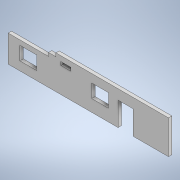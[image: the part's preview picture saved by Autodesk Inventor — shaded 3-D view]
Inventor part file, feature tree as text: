
AUTODESK INVENTOR PART (.ipt)
format: ipt  version: 2020.1 (Build 241239000, 239)  size: 135,680 bytes
history: native  units: in
note: dims shown in document units (in); Inventor stores cm internally (conversion verified against a paired STEP export)
features: extrude x1, sketch x1
ambient origin geometry x8: Origin, YZ Plane, XZ Plane, XY Plane, X Axis, Y Axis, Z Axis, Center Point
bodies: Solid1 (feature_tree)
feature tree (2):
  extrude  "Extrusion1"  Depth=96.0in
  sketch  "Sketch1"  dims[d0=144.0in d1=96.0in d2=26.0in d3=108.0in d4=222.0in d5=120.0in d6=54.0in d7=85.0in d8=180.0in d9=120.0in d10=12.0in d11=36.0in d14=60.0in d15=48.0in d16=60.0in d17=48.0in d18=72.0in d19=126.0in d20=12.0in d21=0.0in d22=572.0in]
